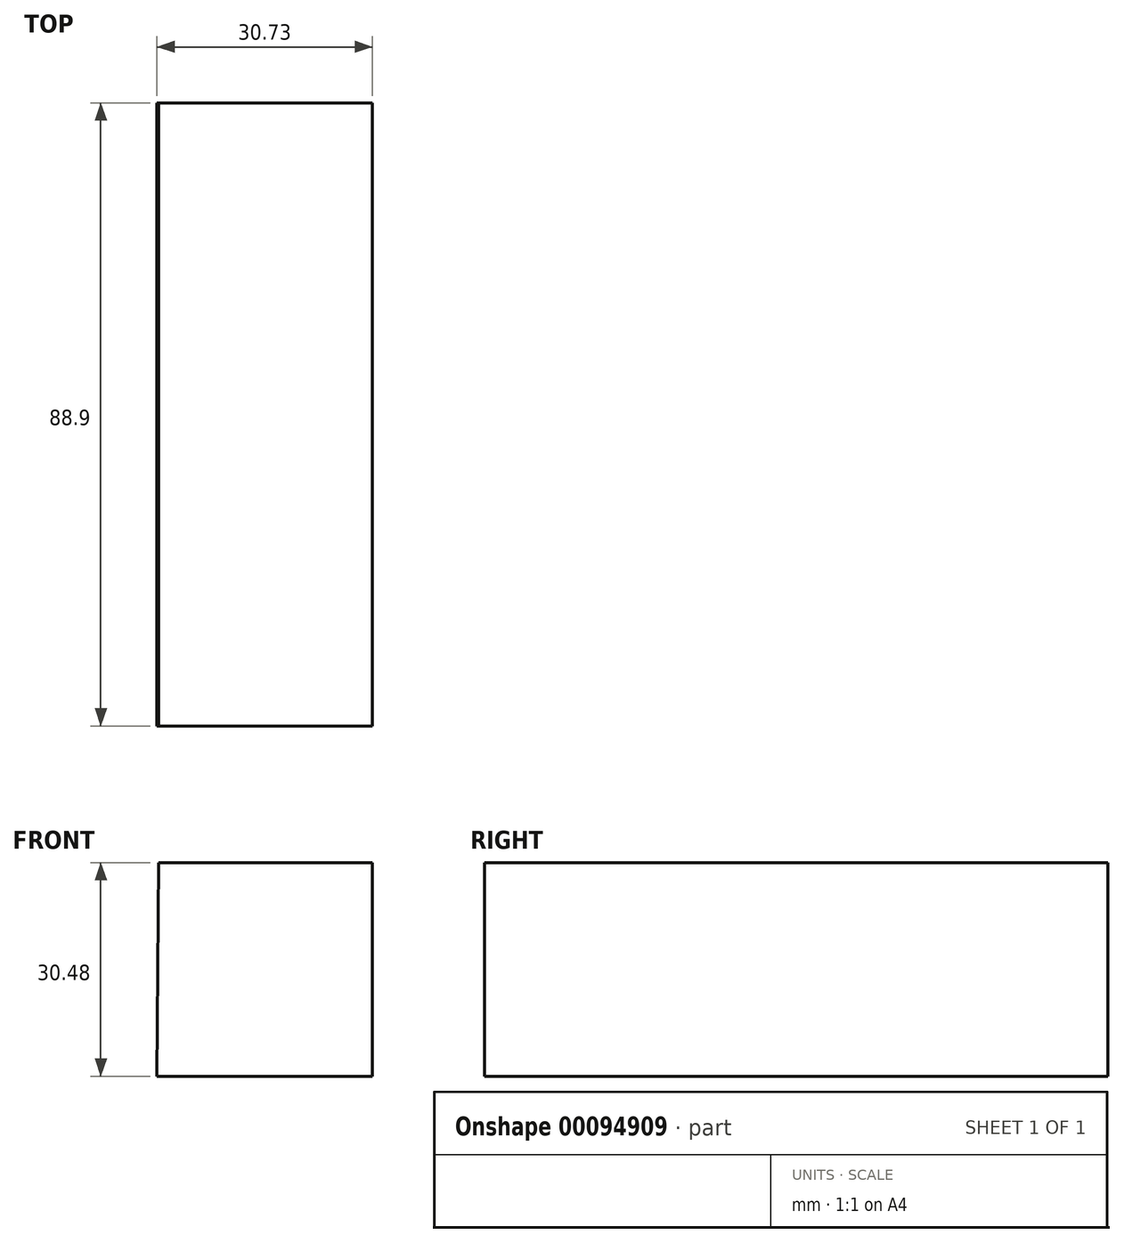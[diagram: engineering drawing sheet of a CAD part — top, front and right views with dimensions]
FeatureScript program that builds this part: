
annotation { "Feature Type Name" : "Feature", "Feature Type Description" : "" }
export const myFeature = defineFeature(function(context is Context, id is Id, definition is map)
    precondition{}
    {
        {
            var Q0;
            Q0=qCreatedBy(makeId("Front.planeOp"),FACE);
            var sketch = newSketch(context, id + "F0", { "sketchPlane" : qUnion([Q0])});
            skLineSegment(sketch, "E0", {"start": v(-43.43, 41.92) * mm, "end": v(-12.95, 41.92) * mm});
            skLineSegment(sketch, "E1", {"start": v(-12.95, 41.92) * mm, "end": v(-12.95, 11.44) * mm});
            skLineSegment(sketch, "E2", {"start": v(-12.95, 11.44) * mm, "end": v(-43.68, 11.44) * mm});
            skLineSegment(sketch, "E3", {"start": v(-43.68, 11.44) * mm, "end": v(-43.43, 41.92) * mm});
            skSolve(sketch);
        }
        {
            var Q0;
            Q0 = qSketchRegion(id + "F0", true);
            extrude(context, id + "F1", {"entities" : qUnion([Q0]), "depth" : 88.9 * mm});
        }
    });
